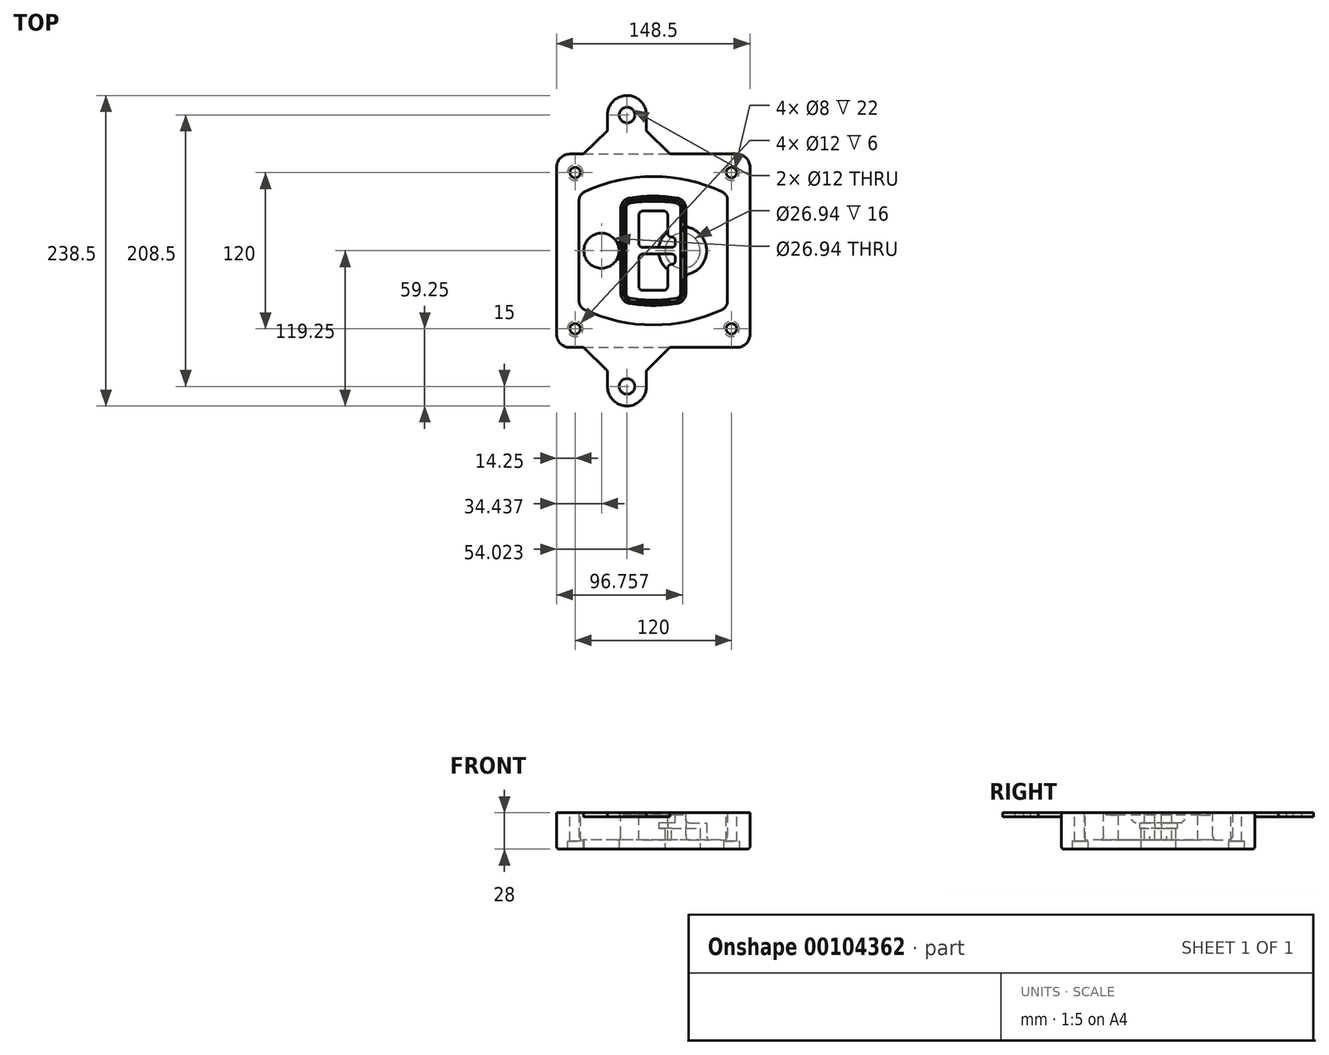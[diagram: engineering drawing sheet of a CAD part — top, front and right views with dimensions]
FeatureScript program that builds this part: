
annotation { "Feature Type Name" : "Feature", "Feature Type Description" : "" }
export const myFeature = defineFeature(function(context is Context, id is Id, definition is map)
    precondition{}
    {
        {
            var Q0;
            Q0=qCreatedBy(makeId("Top.planeOp"),FACE);
            var sketch = newSketch(context, id + "F0", { "sketchPlane" : qUnion([Q0])});
            skPoint(sketch, "E0.rect.middle", {"position": v(0, 0) * mm});
            skLineSegment(sketch, "E1.bottom", {"start": v(-64.25, -74.25) * mm, "end": v(64.25, -74.25) * mm});
            skLineSegment(sketch, "E1.top", {"start": v(-64.25, 74.25) * mm, "end": v(64.25, 74.25) * mm});
            skLineSegment(sketch, "E1.left", {"start": v(-74.25, -64.25) * mm, "end": v(-74.25, 64.25) * mm});
            skLineSegment(sketch, "E1.right", {"start": v(74.25, -64.25) * mm, "end": v(74.25, 64.25) * mm});
            skLineSegment(sketch, "E2", {"start": v(-74.25, 74.25) * mm, "end": v(74.25, -74.25) * mm, "construction": true});
            skLineSegment(sketch, "E3", {"start": v(74.25, 74.25) * mm, "end": v(-74.25, -74.25) * mm, "construction": true});
            skCircle(sketch, "E4", {"center": v(-60, 60) * mm, "radius": 4 * mm});
            skCircle(sketch, "E5", {"center": v(60, 60) * mm, "radius": 4 * mm});
            skCircle(sketch, "E6", {"center": v(60, -60) * mm, "radius": 4 * mm});
            skCircle(sketch, "E7", {"center": v(-60, -60) * mm, "radius": 4 * mm});
            skLineSegment(sketch, "E8", {"start": v(-60, 60) * mm, "end": v(60, 60) * mm, "construction": true});
            skLineSegment(sketch, "E9", {"start": v(60, 60) * mm, "end": v(60, -60) * mm, "construction": true});
            skLineSegment(sketch, "E10", {"start": v(60, -60) * mm, "end": v(-60, -60) * mm, "construction": true});
            skLineSegment(sketch, "E11", {"start": v(-60, -60) * mm, "end": v(-60, 60) * mm, "construction": true});
            skLineSegment(sketch, "E12", {"start": v(-60, 38.83) * mm, "end": v(-60, -38.83) * mm});
            skLineSegment(sketch, "E13", {"start": v(60, 38.83) * mm, "end": v(60, -38.83) * mm});
            skArc(sketch, "E14", {"start": v(54.26, 47.88) * mm, "mid": v(0, 60) * mm, "end": v(-54.26, 47.88) * mm});
            skArc(sketch, "E15", {"start": v(-54.26, -47.88) * mm, "mid": v(0, -60) * mm, "end": v(54.26, -47.88) * mm});
            skLineSegment(sketch, "E16", {"start": v(-60, 0) * mm, "end": v(60, 0) * mm, "construction": true});
            skPoint(sketch, "E17.visualSharp", {"position": v(-60, -45) * mm});
            skArc(sketch, "E17.filletArc", {"start": v(-60, -38.83) * mm, "mid": v(-58.44, -44.2) * mm, "end": v(-54.26, -47.88) * mm});
            skPoint(sketch, "E18.visualSharp", {"position": v(-60, 45) * mm});
            skArc(sketch, "E18.filletArc", {"start": v(-54.26, 47.88) * mm, "mid": v(-58.44, 44.2) * mm, "end": v(-60, 38.83) * mm});
            skPoint(sketch, "E19.visualSharp", {"position": v(60, 45) * mm});
            skArc(sketch, "E19.filletArc", {"start": v(60, 38.83) * mm, "mid": v(58.44, 44.2) * mm, "end": v(54.26, 47.88) * mm});
            skPoint(sketch, "E20.visualSharp", {"position": v(60, -45) * mm});
            skArc(sketch, "E20.filletArc", {"start": v(54.26, -47.88) * mm, "mid": v(58.44, -44.2) * mm, "end": v(60, -38.83) * mm});
            skPoint(sketch, "E21.visualSharp", {"position": v(-74.25, 74.25) * mm});
            skArc(sketch, "E21.filletArc", {"start": v(-64.25, 74.25) * mm, "mid": v(-71.32, 71.32) * mm, "end": v(-74.25, 64.25) * mm});
            skPoint(sketch, "E22.visualSharp", {"position": v(74.25, 74.25) * mm});
            skArc(sketch, "E22.filletArc", {"start": v(74.25, 64.25) * mm, "mid": v(71.32, 71.32) * mm, "end": v(64.25, 74.25) * mm});
            skPoint(sketch, "E23.visualSharp", {"position": v(74.25, -74.25) * mm});
            skArc(sketch, "E23.filletArc", {"start": v(64.25, -74.25) * mm, "mid": v(71.32, -71.32) * mm, "end": v(74.25, -64.25) * mm});
            skPoint(sketch, "E24.visualSharp", {"position": v(-74.25, -74.25) * mm});
            skArc(sketch, "E24.filletArc", {"start": v(-74.25, -64.25) * mm, "mid": v(-71.32, -71.32) * mm, "end": v(-64.25, -74.25) * mm});
            skArc(sketch, "E25.0", {"start": v(57, 38.83) * mm, "mid": v(55.9, 42.58) * mm, "end": v(52.98, 45.17) * mm});
            skLineSegment(sketch, "E25.1", {"start": v(57, 38.83) * mm, "end": v(57, -38.83) * mm});
            skArc(sketch, "E25.2", {"start": v(52.98, -45.17) * mm, "mid": v(55.9, -42.58) * mm, "end": v(57, -38.83) * mm});
            skArc(sketch, "E25.3", {"start": v(-52.98, -45.17) * mm, "mid": v(0, -57) * mm, "end": v(52.98, -45.17) * mm});
            skArc(sketch, "E25.4", {"start": v(-57, -38.83) * mm, "mid": v(-55.9, -42.58) * mm, "end": v(-52.98, -45.17) * mm});
            skArc(sketch, "E25.5", {"start": v(52.98, 45.17) * mm, "mid": v(0, 57) * mm, "end": v(-52.98, 45.17) * mm});
            skLineSegment(sketch, "E25.6", {"start": v(-57, 38.83) * mm, "end": v(-57, -38.83) * mm});
            skArc(sketch, "E25.7", {"start": v(-52.98, 45.17) * mm, "mid": v(-55.9, 42.58) * mm, "end": v(-57, 38.83) * mm});
            skArc(sketch, "E26.0", {"start": v(-55.96, 51.5) * mm, "mid": v(-61.82, 46.33) * mm, "end": v(-64, 38.83) * mm});
            skArc(sketch, "E26.1", {"start": v(55.96, 51.5) * mm, "mid": v(0, 64) * mm, "end": v(-55.96, 51.5) * mm});
            skArc(sketch, "E26.2", {"start": v(64, 38.83) * mm, "mid": v(61.82, 46.33) * mm, "end": v(55.96, 51.5) * mm});
            skLineSegment(sketch, "E26.3", {"start": v(64, 38.83) * mm, "end": v(64, -38.83) * mm});
            skArc(sketch, "E26.4", {"start": v(55.96, -51.5) * mm, "mid": v(61.82, -46.33) * mm, "end": v(64, -38.83) * mm});
            skLineSegment(sketch, "E26.5", {"start": v(-64, 38.83) * mm, "end": v(-64, -38.83) * mm});
            skArc(sketch, "E26.6", {"start": v(-55.96, -51.5) * mm, "mid": v(0, -64) * mm, "end": v(55.96, -51.5) * mm});
            skArc(sketch, "E26.7", {"start": v(-64, -38.83) * mm, "mid": v(-61.82, -46.33) * mm, "end": v(-55.96, -51.5) * mm});
            skSolve(sketch);
        }
        {
            var Q0;
            Q0=makeQuery(id+"F0.imprint","IMPRINT",FACE,{"disambiguationData":[TD([[makeQuery(id+"F0.imprint","IMPRINT",EDGE,{"derivedFrom":sQuery(id+"F0.wireOp",EDGE,"E1.bottom")}),1.0]])]});
            var Q1;
            Q1=makeQuery(id+"F0.imprint","IMPRINT",FACE,{"disambiguationData":[TD([[makeQuery(id+"F0.imprint","IMPRINT",EDGE,{"derivedFrom":sQuery(id+"F0.wireOp",EDGE,"E12")}),1.0]])]});
            var Q2;
            Q2=makeQuery(id+"F0.imprint","IMPRINT",FACE,{"disambiguationData":[TD([[makeQuery(id+"F0.imprint","IMPRINT",EDGE,{"derivedFrom":sQuery(id+"F0.wireOp",EDGE,"E25.0")}),1.0]])]});
            var Q3;
            Q3=makeQuery(id+"F0.imprint","IMPRINT",FACE,{"disambiguationData":[TD([[makeQuery(id+"F0.imprint","IMPRINT",EDGE,{"derivedFrom":sQuery(id+"F0.wireOp",EDGE,"E12")}),-1.0]])]});
            extrude(context, id + "F1", {"entities" : qUnion([Q0, Q1, Q2, Q3]), "oppositeDirection" : true, "depth" : 25 * mm});
        }
        {
            var Q0;
            Q0=makeQuery(id+"F0.imprint","IMPRINT",FACE,{"disambiguationData":[TD([[makeQuery(id+"F0.imprint","IMPRINT",EDGE,{"derivedFrom":sQuery(id+"F0.wireOp",EDGE,"E12")}),1.0]])]});
            extrude(context, id + "F2", {"entities" : qUnion([Q0]), "operationType" : NewBodyOperationType.ADD, "depth" : 3 * mm});
        }
        {
            var Q0;
            Q0=makeQuery(id+"F0.imprint","IMPRINT",FACE,{"disambiguationData":[TD([[makeQuery(id+"F0.imprint","IMPRINT",EDGE,{"derivedFrom":sQuery(id+"F0.wireOp",EDGE,"E25.0")}),1.0]])]});
            extrude(context, id + "F3", {"entities" : qUnion([Q0]), "operationType" : NewBodyOperationType.REMOVE, "oppositeDirection" : true, "depth" : 18 * mm});
        }
        {
            var Q0;
            Q0=makeQuery(id+"F2.opExtrude","CAP_FACE",FACE,{"disambiguationData":[OSD([sQuery(id+"F0.wireOp",EDGE,"E12"),sQuery(id+"F0.wireOp",EDGE,"E13"),sQuery(id+"F0.wireOp",EDGE,"E14"),sQuery(id+"F0.wireOp",EDGE,"E15"),sQuery(id+"F0.wireOp",EDGE,"E17.filletArc"),sQuery(id+"F0.wireOp",EDGE,"E18.filletArc"),sQuery(id+"F0.wireOp",EDGE,"E19.filletArc"),sQuery(id+"F0.wireOp",EDGE,"E20.filletArc"),sQuery(id+"F0.wireOp",EDGE,"E25.0"),sQuery(id+"F0.wireOp",EDGE,"E25.1"),sQuery(id+"F0.wireOp",EDGE,"E25.2"),sQuery(id+"F0.wireOp",EDGE,"E25.3"),sQuery(id+"F0.wireOp",EDGE,"E25.4"),sQuery(id+"F0.wireOp",EDGE,"E25.5"),sQuery(id+"F0.wireOp",EDGE,"E25.6"),sQuery(id+"F0.wireOp",EDGE,"E25.7")])],"isStart":false});
            var sketch = newSketch(context, id + "F4", { "sketchPlane" : qUnion([Q0])});
            skArc(sketch, "E27.0", {"start": v(-18.34, -40.45) * mm, "mid": v(0, -42) * mm, "end": v(18.34, -40.45) * mm});
            skArc(sketch, "E28.0", {"start": v(18.34, 40.45) * mm, "mid": v(0, 42) * mm, "end": v(-18.34, 40.45) * mm});
            skLineSegment(sketch, "E29", {"start": v(-25, 32.57) * mm, "end": v(-25, -32.57) * mm});
            skLineSegment(sketch, "E30", {"start": v(25, 32.57) * mm, "end": v(25, -32.57) * mm});
            skLineSegment(sketch, "E31", {"start": v(-25, 39.1) * mm, "end": v(25, 39.1) * mm, "construction": true});
            skLineSegment(sketch, "E32", {"start": v(-25, -39.1) * mm, "end": v(25, -39.1) * mm, "construction": true});
            skPoint(sketch, "E33.visualSharp", {"position": v(-25, 39.1) * mm});
            skArc(sketch, "E33.filletArc", {"start": v(-18.34, 40.45) * mm, "mid": v(-23.11, 37.73) * mm, "end": v(-25, 32.57) * mm});
            skPoint(sketch, "E34.visualSharp", {"position": v(25, 39.1) * mm});
            skArc(sketch, "E34.filletArc", {"start": v(25, 32.57) * mm, "mid": v(23.11, 37.73) * mm, "end": v(18.34, 40.45) * mm});
            skPoint(sketch, "E35.visualSharp", {"position": v(25, -39.1) * mm});
            skArc(sketch, "E35.filletArc", {"start": v(18.34, -40.45) * mm, "mid": v(23.11, -37.73) * mm, "end": v(25, -32.57) * mm});
            skPoint(sketch, "E36.visualSharp", {"position": v(-25, -39.1) * mm});
            skArc(sketch, "E36.filletArc", {"start": v(-25, -32.57) * mm, "mid": v(-23.11, -37.73) * mm, "end": v(-18.34, -40.45) * mm});
            skArc(sketch, "E37.0", {"start": v(52.98, 45.17) * mm, "mid": v(0, 57) * mm, "end": v(-52.98, 45.17) * mm});
            skArc(sketch, "E37.1", {"start": v(-52.98, 45.17) * mm, "mid": v(-55.9, 42.58) * mm, "end": v(-57, 38.83) * mm});
            skLineSegment(sketch, "E37.2", {"start": v(-57, 38.83) * mm, "end": v(-57, -38.83) * mm});
            skArc(sketch, "E37.3", {"start": v(-57, -38.83) * mm, "mid": v(-55.9, -42.58) * mm, "end": v(-52.98, -45.17) * mm});
            skArc(sketch, "E37.4", {"start": v(-52.98, -45.17) * mm, "mid": v(0, -57) * mm, "end": v(52.98, -45.17) * mm});
            skArc(sketch, "E37.5", {"start": v(52.98, -45.17) * mm, "mid": v(55.9, -42.58) * mm, "end": v(57, -38.83) * mm});
            skLineSegment(sketch, "E37.6", {"start": v(57, 38.83) * mm, "end": v(57, -38.83) * mm});
            skArc(sketch, "E37.7", {"start": v(57, 38.83) * mm, "mid": v(55.9, 42.58) * mm, "end": v(52.98, 45.17) * mm});
            skLineSegment(sketch, "E38.0", {"start": v(23, 32.57) * mm, "end": v(23, -32.57) * mm});
            skArc(sketch, "E38.1", {"start": v(18, -38.48) * mm, "mid": v(21.58, -36.44) * mm, "end": v(23, -32.57) * mm});
            skArc(sketch, "E38.2", {"start": v(-18, -38.48) * mm, "mid": v(0, -40) * mm, "end": v(18, -38.48) * mm});
            skArc(sketch, "E38.3", {"start": v(-23, -32.57) * mm, "mid": v(-21.58, -36.44) * mm, "end": v(-18, -38.48) * mm});
            skLineSegment(sketch, "E38.4", {"start": v(-23, 32.57) * mm, "end": v(-23, -32.57) * mm});
            skArc(sketch, "E38.5", {"start": v(23, 32.57) * mm, "mid": v(21.58, 36.44) * mm, "end": v(18, 38.48) * mm});
            skArc(sketch, "E38.6", {"start": v(-18, 38.48) * mm, "mid": v(-21.58, 36.44) * mm, "end": v(-23, 32.57) * mm});
            skArc(sketch, "E38.7", {"start": v(18, 38.48) * mm, "mid": v(0, 40) * mm, "end": v(-18, 38.48) * mm});
            skArc(sketch, "E39.0", {"start": v(21, 32.57) * mm, "mid": v(20.06, 35.15) * mm, "end": v(17.67, 36.5) * mm});
            skLineSegment(sketch, "E39.1", {"start": v(21, 32.57) * mm, "end": v(21, -32.57) * mm});
            skArc(sketch, "E39.2", {"start": v(17.67, -36.5) * mm, "mid": v(20.06, -35.15) * mm, "end": v(21, -32.57) * mm});
            skArc(sketch, "E39.3", {"start": v(-17.67, -36.5) * mm, "mid": v(0, -38) * mm, "end": v(17.67, -36.5) * mm});
            skArc(sketch, "E39.4", {"start": v(-21, -32.57) * mm, "mid": v(-20.06, -35.15) * mm, "end": v(-17.67, -36.5) * mm});
            skArc(sketch, "E39.5", {"start": v(17.67, 36.5) * mm, "mid": v(0, 38) * mm, "end": v(-17.67, 36.5) * mm});
            skLineSegment(sketch, "E39.6", {"start": v(-21, 32.57) * mm, "end": v(-21, -32.57) * mm});
            skArc(sketch, "E39.7", {"start": v(-17.67, 36.5) * mm, "mid": v(-20.06, 35.15) * mm, "end": v(-21, 32.57) * mm});
            skLineSegment(sketch, "E40", {"start": v(-25, 0) * mm, "end": v(25, 0) * mm, "construction": true});
            skLineSegment(sketch, "E41", {"start": v(-11, 5.5) * mm, "end": v(-11, 27.5) * mm});
            skLineSegment(sketch, "E42", {"start": v(-8, 30.5) * mm, "end": v(8, 30.5) * mm});
            skLineSegment(sketch, "E43", {"start": v(11, 27.5) * mm, "end": v(11, 13.5) * mm});
            skLineSegment(sketch, "E44", {"start": v(14, 10.5) * mm, "end": v(14, 10.5) * mm});
            skLineSegment(sketch, "E45", {"start": v(17, 7.5) * mm, "end": v(17, 5.5) * mm});
            skLineSegment(sketch, "E46", {"start": v(14, 2.5) * mm, "end": v(-8, 2.5) * mm});
            skPoint(sketch, "E47.visualSharp", {"position": v(-11, 30.5) * mm});
            skArc(sketch, "E47.filletArc", {"start": v(-8, 30.5) * mm, "mid": v(-10.12, 29.62) * mm, "end": v(-11, 27.5) * mm});
            skPoint(sketch, "E48.visualSharp", {"position": v(11, 30.5) * mm});
            skArc(sketch, "E48.filletArc", {"start": v(11, 27.5) * mm, "mid": v(10.12, 29.62) * mm, "end": v(8, 30.5) * mm});
            skPoint(sketch, "E49.visualSharp", {"position": v(11, 10.5) * mm});
            skArc(sketch, "E49.filletArc", {"start": v(11, 13.5) * mm, "mid": v(11.88, 11.38) * mm, "end": v(14, 10.5) * mm});
            skPoint(sketch, "E50.visualSharp", {"position": v(17, 10.5) * mm});
            skArc(sketch, "E50.filletArc", {"start": v(17, 7.5) * mm, "mid": v(16.12, 9.62) * mm, "end": v(14, 10.5) * mm});
            skPoint(sketch, "E51.visualSharp", {"position": v(17, 2.5) * mm});
            skArc(sketch, "E51.filletArc", {"start": v(14, 2.5) * mm, "mid": v(16.12, 3.38) * mm, "end": v(17, 5.5) * mm});
            skPoint(sketch, "E52.visualSharp", {"position": v(-11, 2.5) * mm});
            skArc(sketch, "E52.filletArc", {"start": v(-11, 5.5) * mm, "mid": v(-10.12, 3.38) * mm, "end": v(-8, 2.5) * mm});
            skLineSegment(sketch, "E53.0.MirrorCS", {"start": v(14, -2.5) * mm, "end": v(-8, -2.5) * mm});
            skArc(sketch, "E54.0.MirrorCS", {"start": v(-11, -5.5) * mm, "mid": v(-10.12, -3.38) * mm, "end": v(-8, -2.5) * mm});
            skLineSegment(sketch, "E55.0.MirrorCS", {"start": v(-11, -5.5) * mm, "end": v(-11, -27.5) * mm});
            skArc(sketch, "E56.0.MirrorCS", {"start": v(-8, -30.5) * mm, "mid": v(-10.12, -29.62) * mm, "end": v(-11, -27.5) * mm});
            skLineSegment(sketch, "E57.0.MirrorCS", {"start": v(-8, -30.5) * mm, "end": v(8, -30.5) * mm});
            skArc(sketch, "E58.0.MirrorCS", {"start": v(11, -27.5) * mm, "mid": v(10.12, -29.62) * mm, "end": v(8, -30.5) * mm});
            skLineSegment(sketch, "E59.0.MirrorCS", {"start": v(11, -27.5) * mm, "end": v(11, -13.5) * mm});
            skArc(sketch, "E60.0.MirrorCS", {"start": v(11, -13.5) * mm, "mid": v(11.88, -11.38) * mm, "end": v(14, -10.5) * mm});
            skArc(sketch, "E61.0.MirrorCS", {"start": v(17, -7.5) * mm, "mid": v(16.12, -9.62) * mm, "end": v(14, -10.5) * mm});
            skLineSegment(sketch, "E62.0.MirrorCS", {"start": v(17, -7.5) * mm, "end": v(17, -5.5) * mm});
            skArc(sketch, "E63.0.MirrorCS", {"start": v(14, -2.5) * mm, "mid": v(16.12, -3.38) * mm, "end": v(17, -5.5) * mm});
            skSolve(sketch);
        }
        {
            var Q0;
            Q0=makeQuery(id+"F4.imprint","IMPRINT",FACE,{"disambiguationData":[TD([[makeQuery(id+"F4.imprint","IMPRINT",EDGE,{"derivedFrom":sQuery(id+"F4.wireOp",EDGE,"E27.0")}),1.0]])]});
            var Q1;
            Q1=makeQuery(id+"F4.imprint","IMPRINT",FACE,{"disambiguationData":[TD([[makeQuery(id+"F4.imprint","IMPRINT",EDGE,{"derivedFrom":sQuery(id+"F4.wireOp",EDGE,"E38.0")}),-1.0]])]});
            var Q2;
            Q2=makeQuery(id+"F4.imprint","IMPRINT",FACE,{"disambiguationData":[TD([[makeQuery(id+"F4.imprint","IMPRINT",EDGE,{"derivedFrom":sQuery(id+"F4.wireOp",EDGE,"E39.0")}),1.0]])]});
            extrude(context, id + "F5", {"entities" : qUnion([Q0, Q1, Q2]), "operationType" : NewBodyOperationType.ADD, "endBound" : BoundingType.UP_TO_NEXT, "oppositeDirection" : true, "depth" : 25 * mm});
        }
        {
            var Q0;
            Q0=makeQuery(id+"F4.imprint","IMPRINT",FACE,{"disambiguationData":[TD([[makeQuery(id+"F4.imprint","IMPRINT",EDGE,{"derivedFrom":sQuery(id+"F4.wireOp",EDGE,"E38.0")}),-1.0]])]});
            extrude(context, id + "F6", {"entities" : qUnion([Q0]), "operationType" : NewBodyOperationType.REMOVE, "oppositeDirection" : true, "depth" : 2 * mm});
        }
        {
            var Q0;
            Q0=makeQuery(id+"F1.opExtrude","CAP_FACE",FACE,{"disambiguationData":[OSD([sQuery(id+"F0.wireOp",EDGE,"E1.bottom"),sQuery(id+"F0.wireOp",EDGE,"E1.top"),sQuery(id+"F0.wireOp",EDGE,"E1.left"),sQuery(id+"F0.wireOp",EDGE,"E1.right"),sQuery(id+"F0.wireOp",EDGE,"E4"),sQuery(id+"F0.wireOp",EDGE,"E5"),sQuery(id+"F0.wireOp",EDGE,"E6"),sQuery(id+"F0.wireOp",EDGE,"E7"),sQuery(id+"F0.wireOp",EDGE,"E21.filletArc"),sQuery(id+"F0.wireOp",EDGE,"E22.filletArc"),sQuery(id+"F0.wireOp",EDGE,"E23.filletArc"),sQuery(id+"F0.wireOp",EDGE,"E24.filletArc")])],"isStart":false});
            var sketch = newSketch(context, id + "F7", { "sketchPlane" : qUnion([Q0])});
            skCircle(sketch, "E64", {"center": v(22.5, 0) * mm, "radius": 13.47 * mm});
            skCircle(sketch, "E65", {"center": v(-39.81, 0) * mm, "radius": 13.47 * mm});
            skLineSegment(sketch, "E66", {"start": v(74.25, 0) * mm, "end": v(-74.25, 0) * mm});
            skCircle(sketch, "E67", {"center": v(22.5, 0) * mm, "radius": 18.47 * mm});
            skCircle(sketch, "E68", {"center": v(60, -60) * mm, "radius": 6 * mm});
            skCircle(sketch, "E69", {"center": v(-60, -60) * mm, "radius": 6 * mm});
            skCircle(sketch, "E70", {"center": v(-60, 60) * mm, "radius": 6 * mm});
            skCircle(sketch, "E71", {"center": v(60, 60) * mm, "radius": 6 * mm});
            skSolve(sketch);
        }
        {
            var Q0;
            {var subQ1=sQuery(id+"F7.wireOp",EDGE,"E66");var subQ4=sQuery(id+"F7.wireOp",EDGE,"E64");var subQ6=makeQuery(id+"F7.imprint","INTERSECT",VERTEX,{"disambiguationData":[OD(0.0)],"derivedFrom":[subQ4,subQ1]});Q0=makeQuery(id+"F7.imprint","IMPRINT",FACE,{"disambiguationData":[TD([[makeQuery(id+"F7.imprint","IMPRINT",EDGE,{"disambiguationData":[TD([[subQ6,-1.0]])],"derivedFrom":subQ4}),-1.0]])]});}
            var Q1;
            {var subQ0=sQuery(id+"F7.wireOp",EDGE,"E66");var subQ1=sQuery(id+"F7.wireOp",EDGE,"E64");var subQ3=makeQuery(id+"F7.imprint","INTERSECT",VERTEX,{"disambiguationData":[OD(0.0)],"derivedFrom":[subQ1,subQ0]});Q1=makeQuery(id+"F7.imprint","IMPRINT",FACE,{"disambiguationData":[TD([[makeQuery(id+"F7.imprint","IMPRINT",EDGE,{"disambiguationData":[TD([[subQ3,-1.0]])],"derivedFrom":subQ1}),1.0]])]});}
            var Q2;
            {var subQ0=sQuery(id+"F7.wireOp",EDGE,"E66");var subQ1=sQuery(id+"F7.wireOp",EDGE,"E64");var subQ3=makeQuery(id+"F7.imprint","INTERSECT",VERTEX,{"disambiguationData":[OD(0.0)],"derivedFrom":[subQ1,subQ0]});Q2=makeQuery(id+"F7.imprint","IMPRINT",FACE,{"disambiguationData":[TD([[makeQuery(id+"F7.imprint","IMPRINT",EDGE,{"disambiguationData":[TD([[subQ3,1.0]])],"derivedFrom":subQ1}),1.0]])]});}
            var Q3;
            {var subQ1=sQuery(id+"F7.wireOp",EDGE,"E66");var subQ4=sQuery(id+"F7.wireOp",EDGE,"E64");var subQ6=makeQuery(id+"F7.imprint","INTERSECT",VERTEX,{"disambiguationData":[OD(0.0)],"derivedFrom":[subQ4,subQ1]});Q3=makeQuery(id+"F7.imprint","IMPRINT",FACE,{"disambiguationData":[TD([[makeQuery(id+"F7.imprint","IMPRINT",EDGE,{"disambiguationData":[TD([[subQ6,1.0]])],"derivedFrom":subQ4}),-1.0]])]});}
            extrude(context, id + "F8", {"entities" : qUnion([Q0, Q1, Q2, Q3]), "operationType" : NewBodyOperationType.ADD, "oppositeDirection" : true, "depth" : 20 * mm});
        }
        {
            var Q0;
            {var subQ0=sQuery(id+"F7.wireOp",EDGE,"E66");var subQ1=sQuery(id+"F7.wireOp",EDGE,"E64");var subQ3=makeQuery(id+"F7.imprint","INTERSECT",VERTEX,{"disambiguationData":[OD(0.0)],"derivedFrom":[subQ1,subQ0]});Q0=makeQuery(id+"F7.imprint","IMPRINT",FACE,{"disambiguationData":[TD([[makeQuery(id+"F7.imprint","IMPRINT",EDGE,{"disambiguationData":[TD([[subQ3,-1.0]])],"derivedFrom":subQ1}),1.0]])]});}
            var Q1;
            {var subQ0=sQuery(id+"F7.wireOp",EDGE,"E66");var subQ1=sQuery(id+"F7.wireOp",EDGE,"E64");var subQ3=makeQuery(id+"F7.imprint","INTERSECT",VERTEX,{"disambiguationData":[OD(0.0)],"derivedFrom":[subQ1,subQ0]});Q1=makeQuery(id+"F7.imprint","IMPRINT",FACE,{"disambiguationData":[TD([[makeQuery(id+"F7.imprint","IMPRINT",EDGE,{"disambiguationData":[TD([[subQ3,1.0]])],"derivedFrom":subQ1}),1.0]])]});}
            extrude(context, id + "F9", {"entities" : qUnion([Q0, Q1]), "operationType" : NewBodyOperationType.REMOVE, "oppositeDirection" : true, "depth" : 16 * mm});
        }
        {
            var Q0;
            {var subQ0=sQuery(id+"F7.wireOp",EDGE,"E66");var subQ1=sQuery(id+"F7.wireOp",EDGE,"E65");var subQ3=makeQuery(id+"F7.imprint","INTERSECT",VERTEX,{"disambiguationData":[OD(0.0)],"derivedFrom":[subQ1,subQ0]});Q0=makeQuery(id+"F7.imprint","IMPRINT",FACE,{"disambiguationData":[TD([[makeQuery(id+"F7.imprint","IMPRINT",EDGE,{"disambiguationData":[TD([[subQ3,-1.0]])],"derivedFrom":subQ1}),1.0]])]});}
            var Q1;
            {var subQ0=sQuery(id+"F7.wireOp",EDGE,"E66");var subQ1=sQuery(id+"F7.wireOp",EDGE,"E65");var subQ3=makeQuery(id+"F7.imprint","INTERSECT",VERTEX,{"disambiguationData":[OD(0.0)],"derivedFrom":[subQ1,subQ0]});Q1=makeQuery(id+"F7.imprint","IMPRINT",FACE,{"disambiguationData":[TD([[makeQuery(id+"F7.imprint","IMPRINT",EDGE,{"disambiguationData":[TD([[subQ3,1.0]])],"derivedFrom":subQ1}),1.0]])]});}
            extrude(context, id + "F10", {"entities" : qUnion([Q0, Q1]), "operationType" : NewBodyOperationType.REMOVE, "oppositeDirection" : true, "depth" : 25 * mm});
        }
        {
            var Q0;
            Q0=makeQuery(id+"F7.imprint","IMPRINT",FACE,{"disambiguationData":[TD([[makeQuery(id+"F7.imprint","IMPRINT",EDGE,{"derivedFrom":sQuery(id+"F7.wireOp",EDGE,"E68")}),1.0]])]});
            var Q1;
            Q1=makeQuery(id+"F7.imprint","IMPRINT",FACE,{"disambiguationData":[TD([[makeQuery(id+"F7.imprint","IMPRINT",EDGE,{"derivedFrom":makeQuery(id+"F1.opExtrude","CAP_EDGE",EDGE,{"disambiguationData":[OSD([sQuery(id+"F0.wireOp",EDGE,"E5")])],"isStart":false})}),-1.0]])]});
            var Q2;
            Q2=makeQuery(id+"F7.imprint","IMPRINT",FACE,{"disambiguationData":[TD([[makeQuery(id+"F7.imprint","IMPRINT",EDGE,{"derivedFrom":sQuery(id+"F7.wireOp",EDGE,"E69")}),1.0]])]});
            var Q3;
            Q3=makeQuery(id+"F7.imprint","IMPRINT",FACE,{"disambiguationData":[TD([[makeQuery(id+"F7.imprint","IMPRINT",EDGE,{"derivedFrom":makeQuery(id+"F1.opExtrude","CAP_EDGE",EDGE,{"disambiguationData":[OSD([sQuery(id+"F0.wireOp",EDGE,"E4")])],"isStart":false})}),-1.0]])]});
            var Q4;
            Q4=makeQuery(id+"F7.imprint","IMPRINT",FACE,{"disambiguationData":[TD([[makeQuery(id+"F7.imprint","IMPRINT",EDGE,{"derivedFrom":sQuery(id+"F7.wireOp",EDGE,"E70")}),1.0]])]});
            var Q5;
            Q5=makeQuery(id+"F7.imprint","IMPRINT",FACE,{"disambiguationData":[TD([[makeQuery(id+"F7.imprint","IMPRINT",EDGE,{"derivedFrom":makeQuery(id+"F1.opExtrude","CAP_EDGE",EDGE,{"disambiguationData":[OSD([sQuery(id+"F0.wireOp",EDGE,"E7")])],"isStart":false})}),-1.0]])]});
            var Q6;
            Q6=makeQuery(id+"F7.imprint","IMPRINT",FACE,{"disambiguationData":[TD([[makeQuery(id+"F7.imprint","IMPRINT",EDGE,{"derivedFrom":sQuery(id+"F7.wireOp",EDGE,"E71")}),1.0]])]});
            var Q7;
            Q7=makeQuery(id+"F7.imprint","IMPRINT",FACE,{"disambiguationData":[TD([[makeQuery(id+"F7.imprint","IMPRINT",EDGE,{"derivedFrom":makeQuery(id+"F1.opExtrude","CAP_EDGE",EDGE,{"disambiguationData":[OSD([sQuery(id+"F0.wireOp",EDGE,"E6")])],"isStart":false})}),-1.0]])]});
            extrude(context, id + "F11", {"entities" : qUnion([Q0, Q1, Q2, Q3, Q4, Q5, Q6, Q7]), "operationType" : NewBodyOperationType.REMOVE, "oppositeDirection" : true, "depth" : 6 * mm});
        }
        {
            var Q0;
            Q0=makeQuery(id+"F9.boolean.opBoolean","COPY",FACE,{"derivedFrom":makeQuery(id+"F9.opExtrude","CAP_FACE",FACE,{"disambiguationData":[OSD([sQuery(id+"F7.wireOp",EDGE,"E64")])],"isStart":false})});
            var sketch = newSketch(context, id + "F12", { "sketchPlane" : qUnion([Q0])});
            skArc(sketch, "E72.0", {"start": v(11, 14.45) * mm, "mid": v(6.45, 9.13) * mm, "end": v(4.2, 2.5) * mm});
            skArc(sketch, "E72.1", {"start": v(4.2, -2.5) * mm, "mid": v(6.45, -9.13) * mm, "end": v(11, -14.45) * mm});
            skLineSegment(sketch, "E73", {"start": v(4.2, -2.5) * mm, "end": v(14, -2.5) * mm});
            skLineSegment(sketch, "E74.0", {"start": v(14, 2.5) * mm, "end": v(4.2, 2.5) * mm});
            skArc(sketch, "E74.1", {"start": v(14, 2.5) * mm, "mid": v(16.12, 3.38) * mm, "end": v(17, 5.5) * mm});
            skLineSegment(sketch, "E74.2", {"start": v(17, 7.5) * mm, "end": v(17, 5.5) * mm});
            skArc(sketch, "E74.3", {"start": v(17, 7.5) * mm, "mid": v(16.12, 9.62) * mm, "end": v(14, 10.5) * mm});
            skArc(sketch, "E74.4", {"start": v(11, 13.5) * mm, "mid": v(11.88, 11.38) * mm, "end": v(14, 10.5) * mm});
            skLineSegment(sketch, "E74.5", {"start": v(11, 14.45) * mm, "end": v(11, 13.5) * mm});
            skLineSegment(sketch, "E74.7", {"start": v(14, -2.5) * mm, "end": v(4.2, -2.5) * mm});
            skArc(sketch, "E74.8", {"start": v(14, -2.5) * mm, "mid": v(16.12, -3.38) * mm, "end": v(17, -5.5) * mm});
            skLineSegment(sketch, "E74.9", {"start": v(17, -7.5) * mm, "end": v(17, -5.5) * mm});
            skArc(sketch, "E74.10", {"start": v(17, -7.5) * mm, "mid": v(16.12, -9.62) * mm, "end": v(14, -10.5) * mm});
            skArc(sketch, "E74.11", {"start": v(11, -13.5) * mm, "mid": v(11.88, -11.38) * mm, "end": v(14, -10.5) * mm});
            skLineSegment(sketch, "E74.12", {"start": v(11, -14.45) * mm, "end": v(11, -13.5) * mm});
            skPoint(sketch, "E75.orphan", {"position": v(11, -27.5) * mm});
            skPoint(sketch, "E76.orphan", {"position": v(-8, -2.5) * mm});
            skPoint(sketch, "E77.orphan", {"position": v(-8, 2.5) * mm});
            skPoint(sketch, "E78.orphan", {"position": v(11, 27.5) * mm});
            skSolve(sketch);
        }
        {
            var Q0;
            {var subQ7=sQuery(id+"F12.wireOp",EDGE,"E72.0");var subQ14=sQuery(id+"F12.wireOp",EDGE,"E72.1");var subQ16=sQuery(id+"F12.wireOp",EDGE,"E74.1");var subQ18=sQuery(id+"F12.wireOp",EDGE,"E74.8");Q0=qUnion([makeQuery(id+"F12.imprint","IMPRINT",FACE,{"disambiguationData":[TD([[makeQuery(id+"F12.imprint","IMPRINT",EDGE,{"derivedFrom":subQ7}),1.0]])]}),makeQuery(id+"F12.imprint","IMPRINT",FACE,{"disambiguationData":[TD([[makeQuery(id+"F12.imprint","IMPRINT",EDGE,{"derivedFrom":subQ14}),1.0]])]}),makeQuery(id+"F12.imprint","IMPRINT",FACE,{"disambiguationData":[TD([[makeQuery(id+"F12.imprint","IMPRINT",EDGE,{"derivedFrom":subQ16}),1.0]])]}),makeQuery(id+"F12.imprint","IMPRINT",FACE,{"disambiguationData":[TD([[makeQuery(id+"F12.imprint","IMPRINT",EDGE,{"derivedFrom":subQ18}),-1.0]])]})]);}
            var Q1;
            Q1=makeQuery(id+"F5.boolean.opBoolean","SPLIT",FACE,{"disambiguationData":[TD([makeQuery(id+"F5.opExtrude","SWEPT_FACE",FACE,{"disambiguationData":[OSD([sQuery(id+"F4.wireOp",EDGE,"E41")])]})])],"derivedFrom":makeQuery(id+"F3.boolean.opBoolean","COPY",FACE,{"derivedFrom":makeQuery(id+"F3.opExtrude","CAP_FACE",FACE,{"disambiguationData":[OSD([sQuery(id+"F0.wireOp",EDGE,"E25.0"),sQuery(id+"F0.wireOp",EDGE,"E25.1"),sQuery(id+"F0.wireOp",EDGE,"E25.2"),sQuery(id+"F0.wireOp",EDGE,"E25.3"),sQuery(id+"F0.wireOp",EDGE,"E25.4"),sQuery(id+"F0.wireOp",EDGE,"E25.5"),sQuery(id+"F0.wireOp",EDGE,"E25.6"),sQuery(id+"F0.wireOp",EDGE,"E25.7")])],"isStart":false})})});
            extrude(context, id + "F13", {"entities" : qUnion([Q0]), "operationType" : NewBodyOperationType.REMOVE, "endBound" : BoundingType.UP_TO_SURFACE, "endBoundEntityFace" : qUnion([Q1]), "depth" : 25 * mm});
        }
        {
            var Q0;
            Q0=makeQuery(id+"F3.boolean.opBoolean","COPY",EDGE,{"derivedFrom":makeQuery(id+"F3.opExtrude","CAP_EDGE",EDGE,{"disambiguationData":[OSD([sQuery(id+"F0.wireOp",EDGE,"E25.6")])],"isStart":false})});
            var Q1;
            Q1=makeQuery(id+"F8.boolean.opBoolean","INTERSECT",EDGE,{"derivedFrom":[makeQuery(id+"F5.opExtrude","SWEPT_FACE",FACE,{"disambiguationData":[OSD([sQuery(id+"F4.wireOp",EDGE,"E30")])]}),makeQuery(id+"F8.opExtrude","CAP_FACE",FACE,{"disambiguationData":[OSD([sQuery(id+"F7.wireOp",EDGE,"E67")])],"isStart":false})]});
            var Q2;
            Q2=makeQuery(id+"F8.boolean.opBoolean","INTERSECT",EDGE,{"disambiguationData":[OD(1.0)],"derivedFrom":[makeQuery(id+"F5.opExtrude","SWEPT_FACE",FACE,{"disambiguationData":[OSD([sQuery(id+"F4.wireOp",EDGE,"E30")])]}),makeQuery(id+"F8.opExtrude","SWEPT_FACE",FACE,{"disambiguationData":[OSD([sQuery(id+"F7.wireOp",EDGE,"E67")])]})]});
            var Q3;
            {var subQ0=sQuery(id+"F4.wireOp",EDGE,"E30");Q3=makeQuery(id+"F8.boolean.opBoolean","SPLIT",EDGE,{"disambiguationData":[TD([makeQuery(id+"F5.opExtrude","SWEPT_FACE",FACE,{"disambiguationData":[OSD([sQuery(id+"F4.wireOp",EDGE,"E35.filletArc")])]})])],"derivedFrom":makeQuery(id+"F5.opExtrude","CAP_EDGE",EDGE,{"disambiguationData":[OSD([subQ0])],"isStart":false})});}
            var Q4;
            {var subQ0=sQuery(id+"F0.wireOp",EDGE,"E25.7");var subQ1=sQuery(id+"F0.wireOp",EDGE,"E25.1");var subQ2=sQuery(id+"F0.wireOp",EDGE,"E25.6");var subQ3=sQuery(id+"F0.wireOp",EDGE,"E25.5");var subQ4=sQuery(id+"F0.wireOp",EDGE,"E25.4");var subQ5=sQuery(id+"F0.wireOp",EDGE,"E25.0");var subQ6=sQuery(id+"F0.wireOp",EDGE,"E25.2");var subQ7=sQuery(id+"F0.wireOp",EDGE,"E25.3");Q4=makeQuery(id+"F8.boolean.opBoolean","INTERSECT",EDGE,{"derivedFrom":[makeQuery(id+"F5.boolean.opBoolean","SPLIT",FACE,{"disambiguationData":[TD([makeQuery(id+"F2.opExtrude","SWEPT_FACE",FACE,{"disambiguationData":[OSD([subQ5])]})])],"derivedFrom":makeQuery(id+"F3.boolean.opBoolean","COPY",FACE,{"derivedFrom":makeQuery(id+"F3.opExtrude","CAP_FACE",FACE,{"disambiguationData":[OSD([subQ5,subQ1,subQ6,subQ7,subQ4,subQ3,subQ2,subQ0])],"isStart":false})})}),makeQuery(id+"F8.opExtrude","SWEPT_FACE",FACE,{"disambiguationData":[OSD([sQuery(id+"F7.wireOp",EDGE,"E67")])]})]});}
            var Q5;
            Q5=makeQuery(id+"F8.boolean.opBoolean","INTERSECT",EDGE,{"disambiguationData":[OD(0.0)],"derivedFrom":[makeQuery(id+"F5.opExtrude","SWEPT_FACE",FACE,{"disambiguationData":[OSD([sQuery(id+"F4.wireOp",EDGE,"E30")])]}),makeQuery(id+"F8.opExtrude","SWEPT_FACE",FACE,{"disambiguationData":[OSD([sQuery(id+"F7.wireOp",EDGE,"E67")])]})]});
            fillet(context, id + "F14", {"entities" : qUnion([Q0, Q1, Q2, Q3, Q4, Q5]), "radius" : 3 * mm, "tangentPropagation" : true, "allowEdgeOverflow" : false});
        }
        {
            var Q0;
            Q0=makeQuery(id+"F1.opExtrude","CAP_EDGE",EDGE,{"disambiguationData":[OSD([sQuery(id+"F0.wireOp",EDGE,"E1.bottom")])],"isStart":false});
            fillet(context, id + "F15", {"entities" : qUnion([Q0]), "radius" : 2 * mm, "tangentPropagation" : true, "allowEdgeOverflow" : false});
        }
        {
            var Q0;
            {var subQ0=sQuery(id+"F0.wireOp",EDGE,"E22.filletArc");var subQ1=sQuery(id+"F0.wireOp",EDGE,"E7");var subQ2=sQuery(id+"F0.wireOp",EDGE,"E6");var subQ3=sQuery(id+"F0.wireOp",EDGE,"E5");var subQ4=sQuery(id+"F0.wireOp",EDGE,"E4");var subQ5=sQuery(id+"F0.wireOp",EDGE,"E1.bottom");var subQ6=sQuery(id+"F0.wireOp",EDGE,"E21.filletArc");var subQ7=sQuery(id+"F0.wireOp",EDGE,"E1.top");var subQ8=sQuery(id+"F0.wireOp",EDGE,"E1.left");var subQ9=sQuery(id+"F0.wireOp",EDGE,"E1.right");var subQ10=sQuery(id+"F0.wireOp",EDGE,"E23.filletArc");var subQ11=sQuery(id+"F0.wireOp",EDGE,"E24.filletArc");Q0=makeQuery(id+"F2.boolean.opBoolean","SPLIT",FACE,{"disambiguationData":[TD([makeQuery(id+"F1.opExtrude","SWEPT_FACE",FACE,{"disambiguationData":[OSD([subQ5])]})])],"derivedFrom":makeQuery(id+"F1.opExtrude","CAP_FACE",FACE,{"disambiguationData":[OSD([subQ5,subQ7,subQ8,subQ9,subQ4,subQ3,subQ2,subQ1,subQ6,subQ0,subQ10,subQ11])],"isStart":true})});}
            var sketch = newSketch(context, id + "F16", { "sketchPlane" : qUnion([Q0])});
            skLineSegment(sketch, "E79", {"start": v(-53.54, 74.25) * mm, "end": v(-35.22, 92.25) * mm});
            skLineSegment(sketch, "E80", {"start": v(12.77, 74.25) * mm, "end": v(-5.23, 92.25) * mm});
            skLineSegment(sketch, "E81", {"start": v(-35.22, 92.25) * mm, "end": v(-35.22, 103.65) * mm});
            skLineSegment(sketch, "E82", {"start": v(-5.23, 92.25) * mm, "end": v(-5.23, 104.25) * mm});
            skArc(sketch, "E83", {"start": v(-5.23, 104.25) * mm, "mid": v(-20.53, 119.25) * mm, "end": v(-35.22, 103.65) * mm});
            skCircle(sketch, "E84", {"center": v(-20.23, 104.25) * mm, "radius": 6 * mm});
            skLineSegment(sketch, "E85", {"start": v(-74.25, 0) * mm, "end": v(74.25, 0) * mm});
            skLineSegment(sketch, "E86.MirrorCS", {"start": v(-53.54, -74.25) * mm, "end": v(-35.22, -92.25) * mm});
            skLineSegment(sketch, "E87.MirrorCS", {"start": v(-35.22, -92.25) * mm, "end": v(-35.22, -103.65) * mm});
            skArc(sketch, "E88.MirrorCS", {"start": v(-5.23, -104.25) * mm, "mid": v(-20.53, -119.25) * mm, "end": v(-35.22, -103.65) * mm});
            skLineSegment(sketch, "E89.MirrorCS", {"start": v(-5.23, -92.25) * mm, "end": v(-5.23, -104.25) * mm});
            skLineSegment(sketch, "E90.MirrorCS", {"start": v(12.77, -74.25) * mm, "end": v(-5.23, -92.25) * mm});
            skCircle(sketch, "E91.MirrorC", {"center": v(-20.23, -104.25) * mm, "radius": 6 * mm});
            skSolve(sketch);
        }
        {
            var Q0;
            {var subQ0=sQuery(id+"F16.wireOp",EDGE,"E86.MirrorCS");Q0=makeQuery(id+"F16.imprint","IMPRINT",FACE,{"disambiguationData":[TD([[makeQuery(id+"F16.imprint","IMPRINT",EDGE,{"derivedFrom":subQ0}),1.0]])]});}
            var Q1;
            Q1=makeQuery(id+"F16.imprint","IMPRINT",FACE,{"disambiguationData":[TD([[makeQuery(id+"F16.imprint","IMPRINT",EDGE,{"derivedFrom":makeQuery(id+"F1.opExtrude","CAP_EDGE",EDGE,{"disambiguationData":[OSD([sQuery(id+"F0.wireOp",EDGE,"E6")])],"isStart":true})}),-1.0]])]});
            var Q2;
            Q2=makeQuery(id+"F16.imprint","IMPRINT",FACE,{"disambiguationData":[TD([[makeQuery(id+"F16.imprint","IMPRINT",EDGE,{"derivedFrom":makeQuery(id+"F1.opExtrude","CAP_EDGE",EDGE,{"disambiguationData":[OSD([sQuery(id+"F0.wireOp",EDGE,"E4")])],"isStart":true})}),-1.0]])]});
            var Q3;
            {var subQ1=sQuery(id+"F16.wireOp",EDGE,"E79");Q3=makeQuery(id+"F16.imprint","IMPRINT",FACE,{"disambiguationData":[TD([[makeQuery(id+"F16.imprint","IMPRINT",EDGE,{"derivedFrom":subQ1}),-1.0]])]});}
            var Q4;
            Q4=makeQuery(id+"F2.opExtrude","CAP_FACE",FACE,{"disambiguationData":[OSD([sQuery(id+"F0.wireOp",EDGE,"E12"),sQuery(id+"F0.wireOp",EDGE,"E13"),sQuery(id+"F0.wireOp",EDGE,"E14"),sQuery(id+"F0.wireOp",EDGE,"E15"),sQuery(id+"F0.wireOp",EDGE,"E17.filletArc"),sQuery(id+"F0.wireOp",EDGE,"E18.filletArc"),sQuery(id+"F0.wireOp",EDGE,"E19.filletArc"),sQuery(id+"F0.wireOp",EDGE,"E20.filletArc"),sQuery(id+"F0.wireOp",EDGE,"E25.0"),sQuery(id+"F0.wireOp",EDGE,"E25.1"),sQuery(id+"F0.wireOp",EDGE,"E25.2"),sQuery(id+"F0.wireOp",EDGE,"E25.3"),sQuery(id+"F0.wireOp",EDGE,"E25.4"),sQuery(id+"F0.wireOp",EDGE,"E25.5"),sQuery(id+"F0.wireOp",EDGE,"E25.6"),sQuery(id+"F0.wireOp",EDGE,"E25.7")])],"isStart":false});
            extrude(context, id + "F17", {"entities" : qUnion([Q0, Q1, Q2, Q3]), "operationType" : NewBodyOperationType.ADD, "endBound" : BoundingType.UP_TO_SURFACE, "endBoundEntityFace" : qUnion([Q4]), "depth" : 25 * mm});
        }
    });
